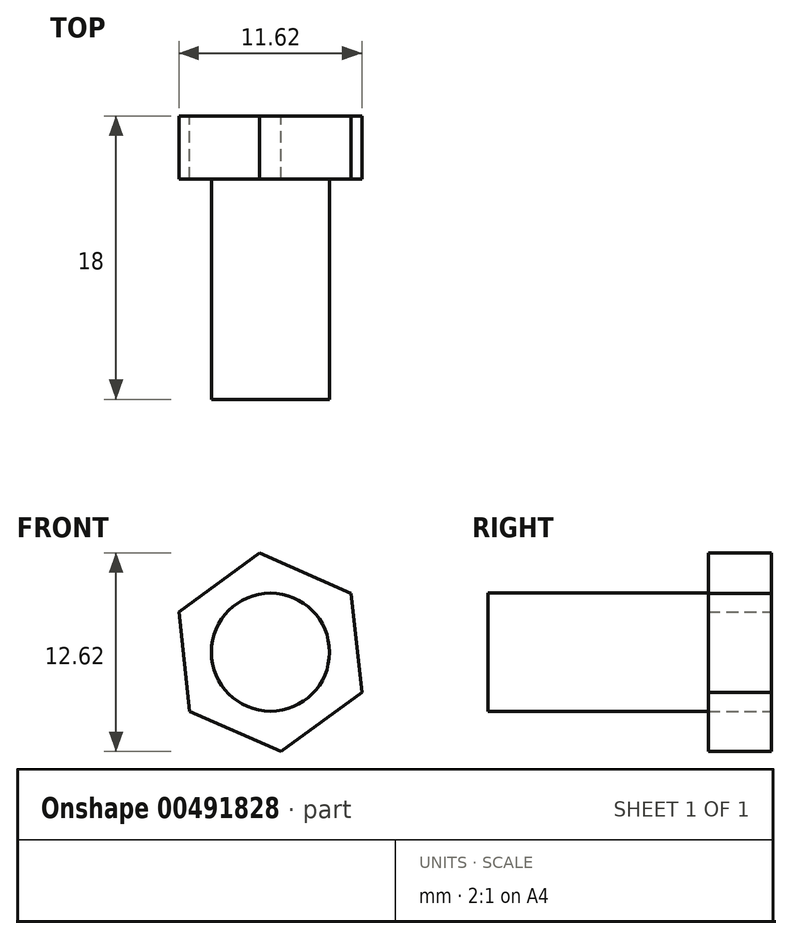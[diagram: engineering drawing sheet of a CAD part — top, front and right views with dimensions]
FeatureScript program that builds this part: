
annotation { "Feature Type Name" : "Feature", "Feature Type Description" : "" }
export const myFeature = defineFeature(function(context is Context, id is Id, definition is map)
    precondition{}
    {
        {
            var Q0;
            Q0=qCreatedBy(makeId("Front.planeOp"),FACE);
            var sketch = newSketch(context, id + "F0", { "sketchPlane" : qUnion([Q0])});
            skCircle(sketch, "E0.cCircle", {"center": v(0, 0) * mm, "radius": 5.5 * mm, "construction": true});
            skLineSegment(sketch, "E0.0", {"start": v(5.8, -2.57) * mm, "end": v(0.68, -6.31) * mm});
            skLineSegment(sketch, "E0.1", {"start": v(0.68, -6.31) * mm, "end": v(-5.13, -3.75) * mm});
            skLineSegment(sketch, "E0.2", {"start": v(-5.13, -3.75) * mm, "end": v(-5.8, 2.57) * mm});
            skLineSegment(sketch, "E0.3", {"start": v(-5.8, 2.57) * mm, "end": v(-0.68, 6.31) * mm});
            skLineSegment(sketch, "E0.4", {"start": v(-0.68, 6.31) * mm, "end": v(5.13, 3.75) * mm});
            skLineSegment(sketch, "E0.5", {"start": v(5.13, 3.75) * mm, "end": v(5.8, -2.57) * mm});
            skPoint(sketch, "E0.0.midPoint", {"position": v(3.25, -4.44) * mm});
            skSolve(sketch);
        }
        {
            var Q0;
            Q0=makeQuery(id+"F0.imprint","IMPRINT",FACE,{"disambiguationData":[TD([[makeQuery(id+"F0.imprint","IMPRINT",EDGE,{"derivedFrom":sQuery(id+"F0.wireOp",EDGE,"0f47cbe5-5944-44aa-9632-a9c43f6134d7.0")}),-1.0]])]});
            var Q1;
            Q1=makeQuery(id+"F0.imprint","IMPRINT",FACE,{"disambiguationData":[TD([[makeQuery(id+"F0.imprint","IMPRINT",EDGE,{"derivedFrom":sQuery(id+"F0.wireOp",EDGE,"E0.0")}),-1.0]])]});
            extrude(context, id + "F1", {"entities" : qUnion([Q0, Q1]), "depth" : 4 * mm});
        }
        {
            var Q0;
            Q0=makeQuery(id+"F1.opExtrude","CAP_FACE",FACE,{"disambiguationData":[OSD([sQuery(id+"F0.wireOp",EDGE,"E0.0"),sQuery(id+"F0.wireOp",EDGE,"E0.1"),sQuery(id+"F0.wireOp",EDGE,"E0.2"),sQuery(id+"F0.wireOp",EDGE,"E0.3"),sQuery(id+"F0.wireOp",EDGE,"E0.4"),sQuery(id+"F0.wireOp",EDGE,"E0.5")])],"isStart":false});
            var sketch = newSketch(context, id + "F2", { "sketchPlane" : qUnion([Q0])});
            skCircle(sketch, "E1", {"center": v(0, 0) * mm, "radius": 3.75 * mm});
            skSolve(sketch);
        }
        {
            var Q0;
            Q0=makeQuery(id+"F2.imprint","IMPRINT",FACE,{"disambiguationData":[TD([[makeQuery(id+"F2.imprint","IMPRINT",EDGE,{"derivedFrom":sQuery(id+"F2.wireOp",EDGE,"E1")}),1.0]])]});
            extrude(context, id + "F3", {"entities" : qUnion([Q0]), "operationType" : NewBodyOperationType.ADD, "depth" : 14 * mm});
        }
    });
